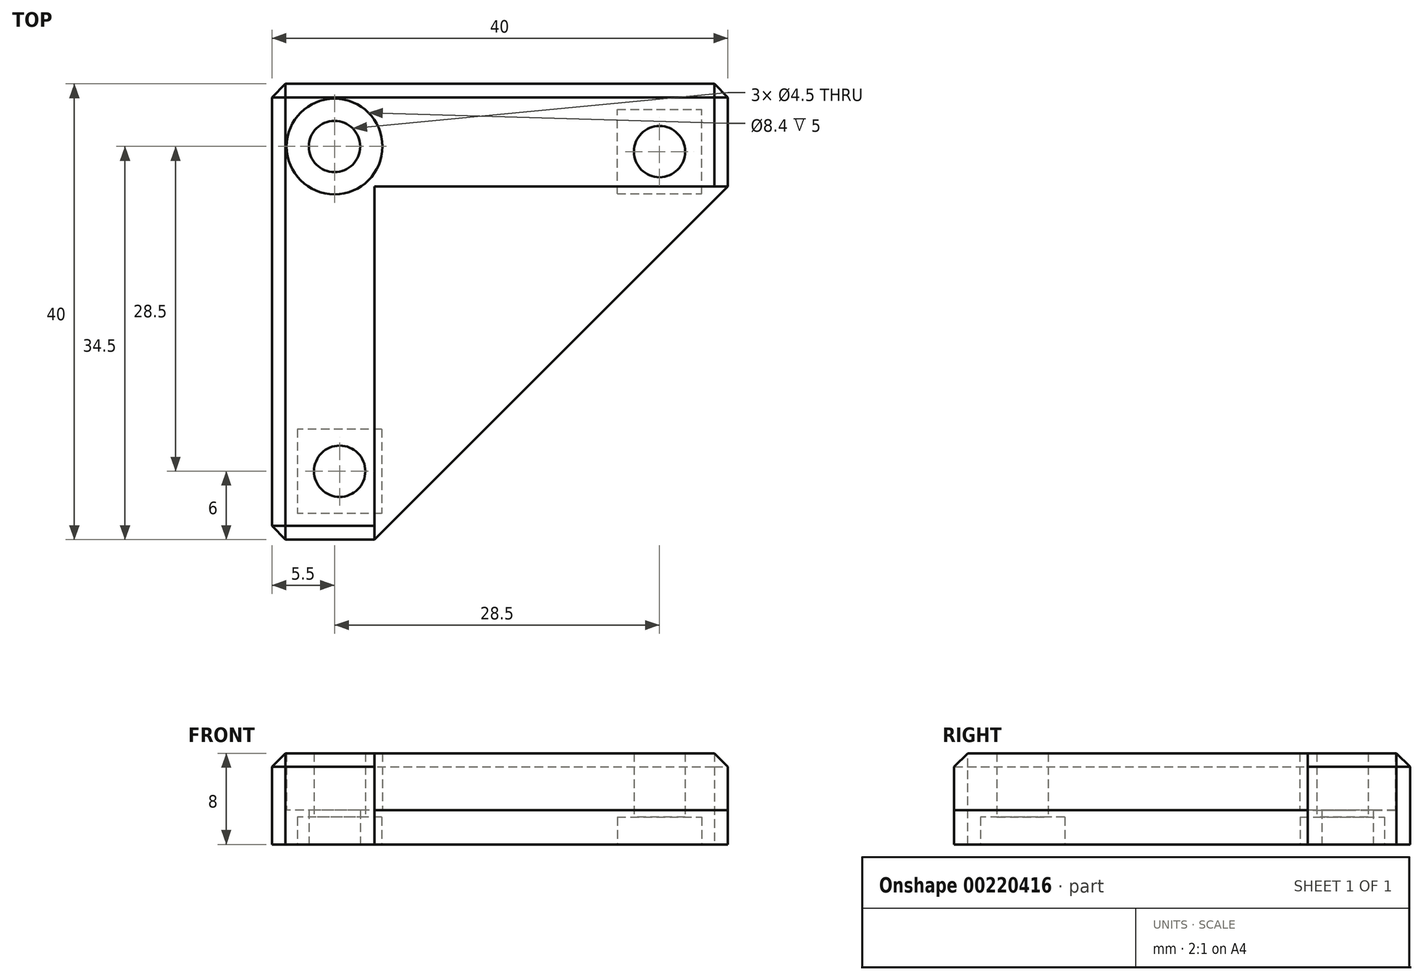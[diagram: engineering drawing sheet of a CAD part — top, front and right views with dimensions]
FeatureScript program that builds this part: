
annotation { "Feature Type Name" : "Feature", "Feature Type Description" : "" }
export const myFeature = defineFeature(function(context is Context, id is Id, definition is map)
    precondition{}
    {
        {
            var Q0;
            Q0=qCreatedBy(makeId("Top.planeOp"),FACE);
            var sketch = newSketch(context, id + "F0", { "sketchPlane" : qUnion([Q0])});
            skCircle(sketch, "E0", {"center": v(0, 0) * mm, "radius": 2.25 * mm});
            skLineSegment(sketch, "E1", {"start": v(-5.5, 5.5) * mm, "end": v(34.5, 5.5) * mm});
            skLineSegment(sketch, "E2", {"start": v(34.5, 5.5) * mm, "end": v(34.5, -3.5) * mm});
            skLineSegment(sketch, "E3", {"start": v(34.5, -3.5) * mm, "end": v(3.5, -34.5) * mm});
            skLineSegment(sketch, "E4", {"start": v(3.5, -34.5) * mm, "end": v(-5.5, -34.5) * mm});
            skLineSegment(sketch, "E5", {"start": v(-5.5, -34.5) * mm, "end": v(-5.5, 5.5) * mm});
            skLineSegment(sketch, "E6", {"start": v(34.5, -3.5) * mm, "end": v(3.5, -3.5) * mm});
            skLineSegment(sketch, "E7", {"start": v(3.5, -3.5) * mm, "end": v(3.5, -34.5) * mm});
            skCircle(sketch, "E8", {"center": v(0, 0) * mm, "radius": 4.2 * mm});
            skCircle(sketch, "E9", {"center": v(28.5, -0.45) * mm, "radius": 2.25 * mm});
            skCircle(sketch, "E10", {"center": v(0.45, -28.5) * mm, "radius": 2.25 * mm});
            skSolve(sketch);
        }
        {
            var Q0;
            Q0=makeQuery(id+"F0.imprint","IMPRINT",FACE,{"disambiguationData":[TD([[makeQuery(id+"F0.imprint","IMPRINT",EDGE,{"derivedFrom":sQuery(id+"F0.wireOp",EDGE,"E1")}),-1.0]])]});
            extrude(context, id + "F1", {"entities" : qUnion([Q0]), "depth" : 8 * mm});
        }
        {
            var Q0;
            Q0=makeQuery(id+"F0.imprint","IMPRINT",FACE,{"disambiguationData":[TD([[makeQuery(id+"F0.imprint","IMPRINT",EDGE,{"derivedFrom":sQuery(id+"F0.wireOp",EDGE,"E3")}),-1.0]])]});
            var Q1;
            Q1=makeQuery(id+"F0.imprint","IMPRINT",FACE,{"disambiguationData":[TD([[makeQuery(id+"F0.imprint","IMPRINT",EDGE,{"derivedFrom":sQuery(id+"F0.wireOp",EDGE,"E0")}),-1.0]])]});
            extrude(context, id + "F2", {"entities" : qUnion([Q0, Q1]), "operationType" : NewBodyOperationType.ADD, "depth" : 3 * mm});
        }
        {
            var Q0;
            {var subQ0=sQuery(id+"F0.wireOp",EDGE,"E7");var subQ1=sQuery(id+"F0.wireOp",EDGE,"E6");var subQ2=sQuery(id+"F0.wireOp",EDGE,"E8");Q0=makeQuery(id+"F2.boolean.opBoolean","MERGE",FACE,{"derivedFrom":[makeQuery(id+"F1.opExtrude","CAP_FACE",FACE,{"disambiguationData":[OSD([sQuery(id+"F0.wireOp",EDGE,"E1"),sQuery(id+"F0.wireOp",EDGE,"E2"),sQuery(id+"F0.wireOp",EDGE,"E4"),sQuery(id+"F0.wireOp",EDGE,"E5"),subQ1,subQ0,subQ2,sQuery(id+"F0.wireOp",EDGE,"E9"),sQuery(id+"F0.wireOp",EDGE,"E10")])],"isStart":true}),makeQuery(id+"F2.opExtrude","CAP_FACE",FACE,{"disambiguationData":[OSD([sQuery(id+"F0.wireOp",EDGE,"E0"),subQ2])],"isStart":true}),makeQuery(id+"F2.opExtrude","CAP_FACE",FACE,{"disambiguationData":[OSD([sQuery(id+"F0.wireOp",EDGE,"E3"),subQ1,subQ0])],"isStart":true})]});}
            var sketch = newSketch(context, id + "F3", { "sketchPlane" : qUnion([Q0])});
            skLineSegment(sketch, "E11.bottom", {"start": v(4.15, 24.8) * mm, "end": v(-3.25, 24.8) * mm});
            skLineSegment(sketch, "E11.top", {"start": v(4.15, 32.2) * mm, "end": v(-3.25, 32.2) * mm});
            skLineSegment(sketch, "E11.left", {"start": v(4.15, 24.8) * mm, "end": v(4.15, 32.2) * mm});
            skLineSegment(sketch, "E11.right", {"start": v(-3.25, 24.8) * mm, "end": v(-3.25, 32.2) * mm});
            skPoint(sketch, "E11.middle", {"position": v(0.45, 28.5) * mm});
            skLineSegment(sketch, "E12.bottom", {"start": v(24.8, 4.15) * mm, "end": v(32.2, 4.15) * mm});
            skLineSegment(sketch, "E12.top", {"start": v(24.8, -3.25) * mm, "end": v(32.2, -3.25) * mm});
            skLineSegment(sketch, "E12.left", {"start": v(24.8, 4.15) * mm, "end": v(24.8, -3.25) * mm});
            skLineSegment(sketch, "E12.right", {"start": v(32.2, 4.15) * mm, "end": v(32.2, -3.25) * mm});
            skPoint(sketch, "E12.middle", {"position": v(28.5, 0.45) * mm});
            skSolve(sketch);
        }
        {
            var Q0;
            Q0=makeQuery(id+"F3.imprint","IMPRINT",FACE,{"disambiguationData":[TD([[makeQuery(id+"F3.imprint","IMPRINT",EDGE,{"derivedFrom":sQuery(id+"F3.wireOp",EDGE,"E11.bottom")}),-1.0]])]});
            var Q1;
            Q1=makeQuery(id+"F3.imprint","IMPRINT",FACE,{"disambiguationData":[TD([[makeQuery(id+"F3.imprint","IMPRINT",EDGE,{"derivedFrom":sQuery(id+"F3.wireOp",EDGE,"E12.bottom")}),-1.0]])]});
            extrude(context, id + "F4", {"entities" : qUnion([Q0, Q1]), "operationType" : NewBodyOperationType.REMOVE, "oppositeDirection" : true, "depth" : 2.4 * mm});
        }
        {
            var Q0;
            Q0=makeQuery(id+"F1.opExtrude","SWEPT_EDGE",EDGE,{"disambiguationData":[OSD([sQuery(id+"F0.wireOp",EDGE,"E1"),sQuery(id+"F0.wireOp",EDGE,"E5")])]});
            var Q1;
            Q1=makeQuery(id+"F1.opExtrude","SWEPT_EDGE",EDGE,{"disambiguationData":[OSD([sQuery(id+"F0.wireOp",EDGE,"E4"),sQuery(id+"F0.wireOp",EDGE,"E5")])]});
            var Q2;
            Q2=makeQuery(id+"F1.opExtrude","SWEPT_EDGE",EDGE,{"disambiguationData":[OSD([sQuery(id+"F0.wireOp",EDGE,"E1"),sQuery(id+"F0.wireOp",EDGE,"E2")])]});
            var Q3;
            Q3=makeQuery(id+"F1.opExtrude","CAP_EDGE",EDGE,{"disambiguationData":[OSD([sQuery(id+"F0.wireOp",EDGE,"E1")])],"isStart":false});
            var Q4;
            Q4=makeQuery(id+"F1.opExtrude","CAP_EDGE",EDGE,{"disambiguationData":[OSD([sQuery(id+"F0.wireOp",EDGE,"E5")])],"isStart":false});
            var Q5;
            Q5=makeQuery(id+"F1.opExtrude","CAP_EDGE",EDGE,{"disambiguationData":[OSD([sQuery(id+"F0.wireOp",EDGE,"E4")])],"isStart":false});
            var Q6;
            Q6=makeQuery(id+"F1.opExtrude","CAP_EDGE",EDGE,{"disambiguationData":[OSD([sQuery(id+"F0.wireOp",EDGE,"E2")])],"isStart":false});
            chamfer(context, id + "F5", {"entities" : qUnion([Q0, Q1, Q2, Q3, Q4, Q5, Q6]), "width" : 1.2 * mm, "tangentPropagation" : true});
        }
    });
